# Revit family: 11. Wichmann TW90 Faltbox
name_source: partatom
category: HLS-Bauteile
revit_build: Autodesk Revit 2018 (Build: 20170223_1515(x64)
units: mm (PartAtom-declared; Revit-internal decimal feet)

## family parameters
Basisbauteil = Wand
Beim Laden mit Abzugskörper schneiden = Nein
Bemaßung runder Anschluss = Durchmesser verwenden
Gemeinsam genutzt = Nein
Immer vertikal = Ja
Raumberechnungspunkt = Nein
Teiletyp = Normal

## types (10) — shared parameters
Abst = 45 mm  [stored 0.147638 ft]
Höhe Außenmaß = 60 mm  [stored 0.19685 ft]
Höhe Rohbauöffnung = 90 mm  [stored 0.295276 ft]
Höhe UK Durchbruch = 1680 mm
Rohbauöffnung = Ja

## per-type parameters (varying)
| type | Bautiefe | Breite Außenmaß | Breite Innenmaß | Breite Rohbauöffnung | HAN | Höhe Innenmaß |
| TW90 Faltbox, 60x160x150 mm | 150 mm  [stored 0.492126 ft] | 280 mm | 250 mm | 300 mm | FB60160150 | 37 mm |
| TW90 Faltbox, 60x240x150 mm | 150 mm  [stored 0.492126 ft] | 240 mm | 210 mm | 260 mm | FB60240150 | 35 mm  [stored 0.114829 ft] |
| TW90 Faltbox, 60x280x125 mm | 125 mm | 280 mm | 250 mm | 300 mm | FB60280125 | 35 mm  [stored 0.114829 ft] |
| TW90 Faltbox, 60x280x150 mm | 150 mm  [stored 0.492126 ft] | 280 mm | 250 mm | 300 mm | FB60280150 | 37 mm |
| TW90 Faltbox, 60x120x125 mm | 125 mm | 120 mm | 90 mm  [stored 0.295276 ft] | 140 mm | FB60120125 | 35 mm  [stored 0.114829 ft] |
| TW90 Faltbox, 60x120x150 mm | 150 mm  [stored 0.492126 ft] | 120 mm | 90 mm  [stored 0.295276 ft] | 140 mm | FB60120150 | 35 mm  [stored 0.114829 ft] |
| TW90 Faltbox, 60x160x125 mm | 125 mm | 160 mm | 130 mm | 180 mm | FB60160125 | 35 mm  [stored 0.114829 ft] |
| TW90 Faltbox, 60x200x125 mm | 125 mm | 200 mm  [stored 0.656168 ft] | 170 mm  [stored 0.557743 ft] | 220 mm  [stored 0.721785 ft] | FB60200125 | 35 mm  [stored 0.114829 ft] |
| TW90 Faltbox, 60x200x150 mm | 150 mm  [stored 0.492126 ft] | 200 mm  [stored 0.656168 ft] | 170 mm  [stored 0.557743 ft] | 220 mm  [stored 0.721785 ft] | FB60200150 | 35 mm  [stored 0.114829 ft] |
| TW90 Faltbox, 60x240x125 mm | 125 mm | 240 mm | 210 mm | 260 mm | FB60240125 | 35 mm  [stored 0.114829 ft] |

note: [stored X ft] marks values corroborated as IEEE doubles in the binary element streams (Revit-internal decimal feet)
